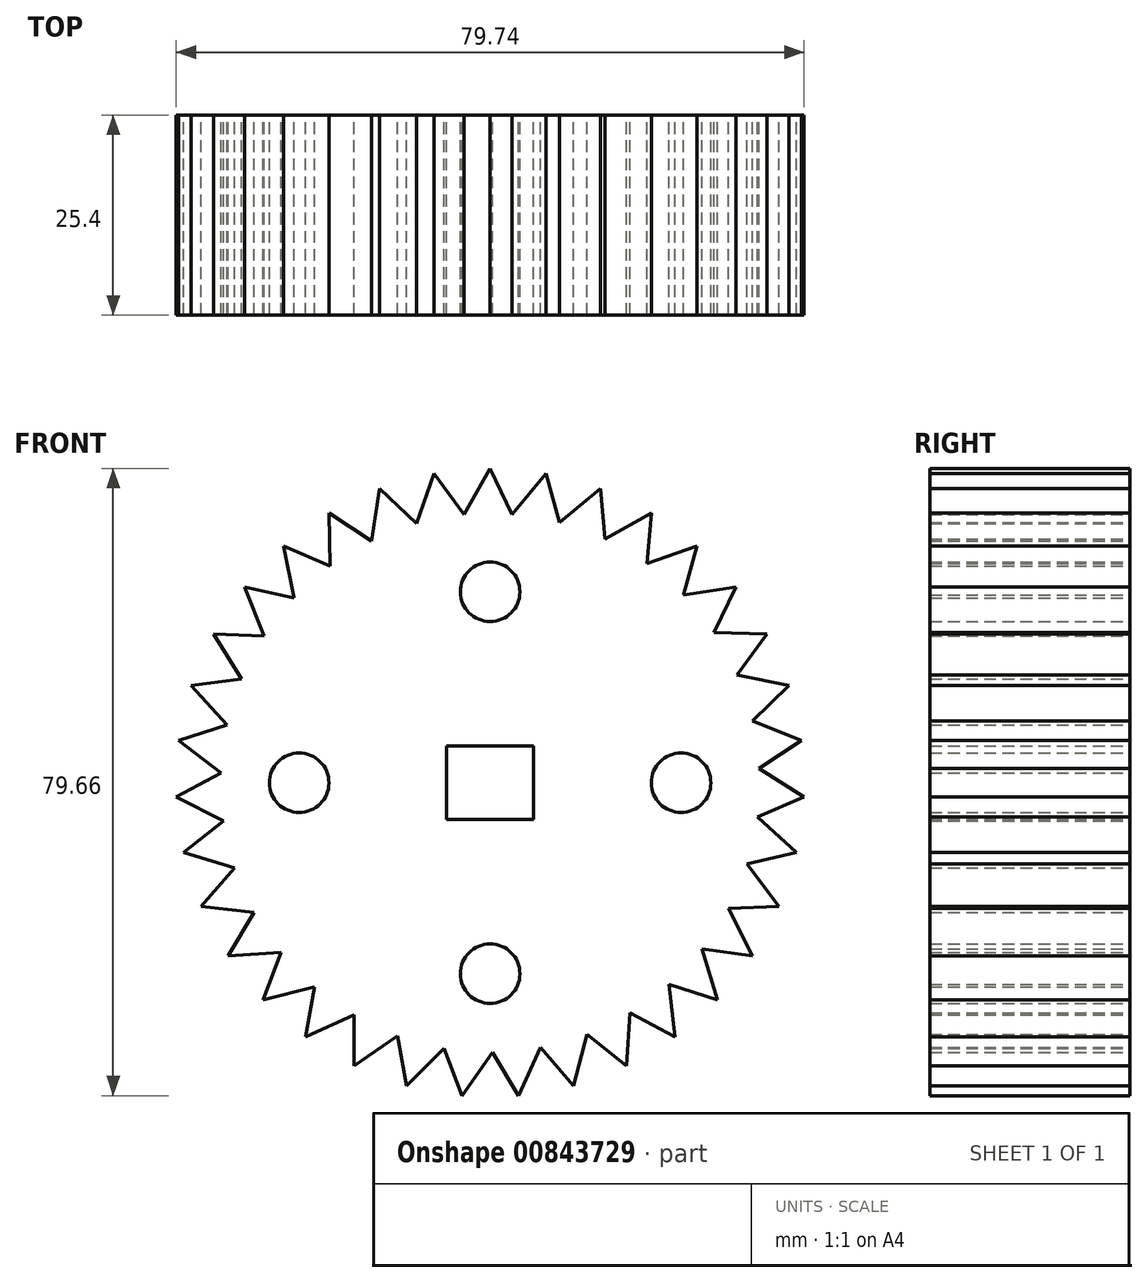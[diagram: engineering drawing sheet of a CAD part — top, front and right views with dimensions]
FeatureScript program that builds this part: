
annotation { "Feature Type Name" : "Feature", "Feature Type Description" : "" }
export const myFeature = defineFeature(function(context is Context, id is Id, definition is map)
    precondition{}
    {
        {
            var Q0;
            Q0=qCreatedBy(makeId("Front.planeOp"),FACE);
            var sketch = newSketch(context, id + "F0", { "sketchPlane" : qUnion([Q0])});
            skLineSegment(sketch, "E0.bottom", {"start": v(5.53, 4.68) * mm, "end": v(-5.53, 4.68) * mm});
            skLineSegment(sketch, "E0.top", {"start": v(5.53, -4.68) * mm, "end": v(-5.53, -4.68) * mm});
            skLineSegment(sketch, "E0.left", {"start": v(5.53, 4.68) * mm, "end": v(5.53, -4.68) * mm});
            skLineSegment(sketch, "E0.right", {"start": v(-5.53, 4.68) * mm, "end": v(-5.53, -4.68) * mm});
            skPoint(sketch, "E0.middle", {"position": v(0, 0) * mm});
            skLineSegment(sketch, "E1.bottom", {"start": v(9.22, 8.65) * mm, "end": v(-9.22, 8.65) * mm});
            skLineSegment(sketch, "E1.top", {"start": v(9.22, -8.65) * mm, "end": v(-9.22, -8.65) * mm});
            skLineSegment(sketch, "E1.left", {"start": v(9.22, 8.65) * mm, "end": v(9.22, -8.65) * mm});
            skLineSegment(sketch, "E1.right", {"start": v(-9.22, 8.65) * mm, "end": v(-9.22, -8.65) * mm});
            skLineSegment(sketch, "E2", {"start": v(-2.98, 8.65) * mm, "end": v(-2.98, 16.88) * mm});
            skLineSegment(sketch, "E3", {"start": v(2.98, 8.65) * mm, "end": v(2.98, 16.88) * mm});
            skCircle(sketch, "E4", {"center": v(0, 24.26) * mm, "radius": 3.78 * mm});
            skLineSegment(sketch, "E5.1.0", {"start": v(-8.65, 2.98) * mm, "end": v(-16.88, 2.98) * mm});
            skLineSegment(sketch, "E5.1.1", {"start": v(-8.65, -2.98) * mm, "end": v(-16.88, -2.98) * mm});
            skCircle(sketch, "E5.1.2", {"center": v(-24.26, 0) * mm, "radius": 3.78 * mm});
            skLineSegment(sketch, "E5.2.0", {"start": v(-2.98, -8.65) * mm, "end": v(-2.98, -16.88) * mm});
            skLineSegment(sketch, "E5.2.1", {"start": v(2.98, -8.65) * mm, "end": v(2.98, -16.88) * mm});
            skCircle(sketch, "E5.2.2", {"center": v(0, -24.26) * mm, "radius": 3.78 * mm});
            skLineSegment(sketch, "E5.3.0", {"start": v(8.65, -2.98) * mm, "end": v(16.88, -2.98) * mm});
            skLineSegment(sketch, "E5.3.1", {"start": v(8.65, 2.98) * mm, "end": v(16.88, 2.98) * mm});
            skCircle(sketch, "E5.3.2", {"center": v(24.26, 0) * mm, "radius": 3.78 * mm});
            skCircle(sketch, "E6", {"center": v(0, 23.4) * mm, "radius": 7.16 * mm});
            skPoint(sketch, "E6.third.point", {"position": v(0, 30.56) * mm});
            skCircle(sketch, "E7.1.0", {"center": v(-23.4, 0) * mm, "radius": 7.16 * mm});
            skCircle(sketch, "E7.2.0", {"center": v(0, -23.4) * mm, "radius": 7.16 * mm});
            skCircle(sketch, "E7.3.0", {"center": v(23.4, 0) * mm, "radius": 7.16 * mm});
            skCircle(sketch, "E8", {"center": v(0, 0) * mm, "radius": 33.5 * mm});
            skLineSegment(sketch, "E9", {"start": v(-3.78, 33.28) * mm, "end": v(0, 39.91) * mm});
            skLineSegment(sketch, "E10", {"start": v(0, 39.91) * mm, "end": v(3.16, 33.34) * mm});
            skLineSegment(sketch, "E11.1.0", {"start": v(-7.13, 39.27) * mm, "end": v(-2.84, 33.37) * mm});
            skLineSegment(sketch, "E11.1.1", {"start": v(-9.66, 32.07) * mm, "end": v(-7.13, 39.27) * mm});
            skLineSegment(sketch, "E11.2.0", {"start": v(-14.02, 37.37) * mm, "end": v(-8.76, 32.33) * mm});
            skLineSegment(sketch, "E11.2.1", {"start": v(-15.24, 29.83) * mm, "end": v(-14.02, 37.37) * mm});
            skLineSegment(sketch, "E11.3.0", {"start": v(-20.47, 34.26) * mm, "end": v(-14.39, 30.25) * mm});
            skLineSegment(sketch, "E11.3.1", {"start": v(-20.32, 26.63) * mm, "end": v(-20.47, 34.26) * mm});
            skLineSegment(sketch, "E11.4.0", {"start": v(-26.26, 30.06) * mm, "end": v(-19.56, 27.2) * mm});
            skLineSegment(sketch, "E11.4.1", {"start": v(-24.74, 22.57) * mm, "end": v(-26.26, 30.06) * mm});
            skLineSegment(sketch, "E11.5.0", {"start": v(-31.2, 24.89) * mm, "end": v(-24.1, 23.26) * mm});
            skLineSegment(sketch, "E11.5.1", {"start": v(-28.38, 17.8) * mm, "end": v(-31.2, 24.89) * mm});
            skLineSegment(sketch, "E11.6.0", {"start": v(-35.15, 18.91) * mm, "end": v(-27.86, 18.59) * mm});
            skLineSegment(sketch, "E11.6.1", {"start": v(-31.1, 12.44) * mm, "end": v(-35.15, 18.91) * mm});
            skLineSegment(sketch, "E11.7.0", {"start": v(-37.96, 12.33) * mm, "end": v(-30.74, 13.31) * mm});
            skLineSegment(sketch, "E11.7.1", {"start": v(-32.82, 6.69) * mm, "end": v(-37.96, 12.33) * mm});
            skLineSegment(sketch, "E11.8.0", {"start": v(-39.55, 5.36) * mm, "end": v(-32.62, 7.6) * mm});
            skLineSegment(sketch, "E11.8.1", {"start": v(-33.49, 0.72) * mm, "end": v(-39.55, 5.36) * mm});
            skLineSegment(sketch, "E11.9.0", {"start": v(-39.87, -1.8) * mm, "end": v(-33.45, 1.66) * mm});
            skLineSegment(sketch, "E11.9.1", {"start": v(-33.08, -5.27) * mm, "end": v(-39.87, -1.8) * mm});
            skLineSegment(sketch, "E12.2.10.0", {"start": v(-38.91, -8.88) * mm, "end": v(-33.21, -4.34) * mm});
            skLineSegment(sketch, "E12.3.10.0", {"start": v(-31.6, -11.1) * mm, "end": v(-38.91, -8.88) * mm});
            skLineSegment(sketch, "E12.2.11.0", {"start": v(-36.7, -15.69) * mm, "end": v(-31.9, -10.2) * mm});
            skLineSegment(sketch, "E12.3.11.0", {"start": v(-29.12, -16.56) * mm, "end": v(-36.7, -15.69) * mm});
            skLineSegment(sketch, "E12.2.12.0", {"start": v(-33.31, -21.99) * mm, "end": v(-29.57, -15.73) * mm});
            skLineSegment(sketch, "E12.3.12.0", {"start": v(-25.7, -21.5) * mm, "end": v(-33.31, -21.99) * mm});
            skLineSegment(sketch, "E12.2.13.0", {"start": v(-28.85, -27.58) * mm, "end": v(-26.29, -20.76) * mm});
            skLineSegment(sketch, "E12.3.13.0", {"start": v(-21.44, -25.73) * mm, "end": v(-28.85, -27.58) * mm});
            skLineSegment(sketch, "E12.2.14.0", {"start": v(-23.46, -32.3) * mm, "end": v(-22.16, -25.12) * mm});
            skLineSegment(sketch, "E12.3.14.0", {"start": v(-16.5, -29.15) * mm, "end": v(-23.46, -32.3) * mm});
            skLineSegment(sketch, "E12.2.15.0", {"start": v(-17.32, -35.96) * mm, "end": v(-17.32, -28.67) * mm});
            skLineSegment(sketch, "E12.3.15.0", {"start": v(-11.03, -31.63) * mm, "end": v(-17.32, -35.96) * mm});
            skLineSegment(sketch, "E12.2.16.0", {"start": v(-10.62, -38.47) * mm, "end": v(-11.92, -31.3) * mm});
            skLineSegment(sketch, "E12.3.16.0", {"start": v(-5.2, -33.09) * mm, "end": v(-10.62, -38.47) * mm});
            skLineSegment(sketch, "E12.2.17.0", {"start": v(-3.58, -39.75) * mm, "end": v(-6.14, -32.93) * mm});
            skLineSegment(sketch, "E12.3.17.0", {"start": v(0.78, -33.48) * mm, "end": v(-3.58, -39.75) * mm});
            skLineSegment(sketch, "E12.2.18.0", {"start": v(3.58, -39.75) * mm, "end": v(-0.16, -33.5) * mm});
            skLineSegment(sketch, "E12.3.18.0", {"start": v(6.75, -32.8) * mm, "end": v(3.58, -39.75) * mm});
            skLineSegment(sketch, "E12.2.19.0", {"start": v(10.62, -38.47) * mm, "end": v(5.82, -32.98) * mm});
            skLineSegment(sketch, "E12.3.19.0", {"start": v(12.5, -31.07) * mm, "end": v(10.62, -38.47) * mm});
            skLineSegment(sketch, "E12.2.20.0", {"start": v(17.32, -35.96) * mm, "end": v(11.62, -31.41) * mm});
            skLineSegment(sketch, "E12.3.20.0", {"start": v(17.85, -28.34) * mm, "end": v(17.32, -35.96) * mm});
            skLineSegment(sketch, "E12.2.21.0", {"start": v(23.46, -32.3) * mm, "end": v(17.04, -28.83) * mm});
            skLineSegment(sketch, "E12.3.21.0", {"start": v(22.62, -24.7) * mm, "end": v(23.46, -32.3) * mm});
            skLineSegment(sketch, "E12.2.22.0", {"start": v(28.85, -27.58) * mm, "end": v(21.92, -25.33) * mm});
            skLineSegment(sketch, "E12.3.22.0", {"start": v(26.67, -20.26) * mm, "end": v(28.85, -27.58) * mm});
            skLineSegment(sketch, "E12.2.23.0", {"start": v(33.31, -21.99) * mm, "end": v(26.09, -21) * mm});
            skLineSegment(sketch, "E12.3.23.0", {"start": v(29.86, -15.18) * mm, "end": v(33.31, -21.99) * mm});
            skLineSegment(sketch, "E12.2.24.0", {"start": v(36.7, -15.69) * mm, "end": v(29.42, -16.01) * mm});
            skLineSegment(sketch, "E12.3.24.0", {"start": v(32.09, -9.6) * mm, "end": v(36.7, -15.69) * mm});
            skLineSegment(sketch, "E12.2.25.0", {"start": v(38.91, -8.88) * mm, "end": v(31.8, -10.5) * mm});
            skLineSegment(sketch, "E12.3.25.0", {"start": v(33.29, -3.72) * mm, "end": v(38.91, -8.88) * mm});
            skLineSegment(sketch, "E12.2.26.0", {"start": v(39.87, -1.8) * mm, "end": v(33.17, -4.65) * mm});
            skLineSegment(sketch, "E12.3.26.0", {"start": v(33.42, 2.29) * mm, "end": v(39.87, -1.8) * mm});
            skLineSegment(sketch, "E12.2.27.0", {"start": v(39.55, 5.36) * mm, "end": v(33.47, 1.34) * mm});
            skLineSegment(sketch, "E12.3.27.0", {"start": v(32.47, 8.22) * mm, "end": v(39.55, 5.36) * mm});
            skLineSegment(sketch, "E12.2.28.0", {"start": v(37.96, 12.33) * mm, "end": v(32.69, 7.3) * mm});
            skLineSegment(sketch, "E12.3.28.0", {"start": v(30.48, 13.88) * mm, "end": v(37.96, 12.33) * mm});
            skLineSegment(sketch, "E12.2.29.0", {"start": v(35.15, 18.91) * mm, "end": v(30.86, 13.02) * mm});
            skLineSegment(sketch, "E12.3.29.0", {"start": v(27.51, 19.1) * mm, "end": v(35.15, 18.91) * mm});
            skLineSegment(sketch, "E13.2.30.0", {"start": v(31.2, 24.89) * mm, "end": v(28.04, 18.32) * mm});
            skLineSegment(sketch, "E13.3.30.0", {"start": v(23.66, 23.7) * mm, "end": v(31.2, 24.89) * mm});
            skLineSegment(sketch, "E13.2.31.0", {"start": v(26.26, 30.06) * mm, "end": v(24.32, 23.03) * mm});
            skLineSegment(sketch, "E13.3.31.0", {"start": v(19.05, 27.55) * mm, "end": v(26.26, 30.06) * mm});
            skLineSegment(sketch, "E13.2.32.0", {"start": v(20.47, 34.26) * mm, "end": v(19.82, 27) * mm});
            skLineSegment(sketch, "E13.3.32.0", {"start": v(13.82, 30.5) * mm, "end": v(20.47, 34.26) * mm});
            skLineSegment(sketch, "E13.2.33.0", {"start": v(14.02, 37.37) * mm, "end": v(14.68, 30.1) * mm});
            skLineSegment(sketch, "E13.3.33.0", {"start": v(8.15, 32.49) * mm, "end": v(14.02, 37.37) * mm});
            skLineSegment(sketch, "E13.2.34.0", {"start": v(7.13, 39.27) * mm, "end": v(9.07, 32.24) * mm});
            skLineSegment(sketch, "E13.3.34.0", {"start": v(2.22, 33.42) * mm, "end": v(7.13, 39.27) * mm});
            skSolve(sketch);
        }
        {
            var Q0;
            Q0 = qSketchRegion(id + "F0", true);
            var Q1;
            {var subQ23=sQuery(id+"F0.wireOp",EDGE,"E2");Q1=makeQuery(id+"F0.imprint","IMPRINT",FACE,{"disambiguationData":[TD([[makeQuery(id+"F0.imprint","IMPRINT",EDGE,{"derivedFrom":subQ23}),1.0]])]});}
            var Q2;
            Q2=makeQuery(id+"F0.imprint","IMPRINT",FACE,{"disambiguationData":[TD([[makeQuery(id+"F0.imprint","IMPRINT",EDGE,{"derivedFrom":sQuery(id+"F0.wireOp",EDGE,"E0.bottom")}),-1.0]])]});
            var Q3;
            {var subQ0=sQuery(id+"F0.wireOp",EDGE,"E5.1.0");var subQ1=sQuery(id+"F0.wireOp",EDGE,"E1.right");var subQ2=makeQuery(id+"F0.imprint","INTERSECT",VERTEX,{"derivedFrom":[subQ1,subQ0]});Q3=makeQuery(id+"F0.imprint","IMPRINT",FACE,{"disambiguationData":[TD([[makeQuery(id+"F0.imprint","IMPRINT",EDGE,{"disambiguationData":[TD([[subQ2,-1.0]])],"derivedFrom":subQ1}),-1.0]])]});}
            var Q4;
            Q4=makeQuery(id+"F0.imprint","IMPRINT",FACE,{"disambiguationData":[TD([[makeQuery(id+"F0.imprint","IMPRINT",EDGE,{"derivedFrom":sQuery(id+"F0.wireOp",EDGE,"E5.1.2")}),-1.0]])]});
            var Q5;
            {var subQ0=sQuery(id+"F0.wireOp",EDGE,"E5.2.0");Q5=makeQuery(id+"F0.imprint","IMPRINT",FACE,{"disambiguationData":[TD([[makeQuery(id+"F0.imprint","IMPRINT",EDGE,{"derivedFrom":subQ0}),1.0]])]});}
            var Q6;
            {var subQ0=sQuery(id+"F0.wireOp",EDGE,"E5.3.1");var subQ1=sQuery(id+"F0.wireOp",EDGE,"E1.left");var subQ2=makeQuery(id+"F0.imprint","INTERSECT",VERTEX,{"derivedFrom":[subQ1,subQ0]});Q6=makeQuery(id+"F0.imprint","IMPRINT",FACE,{"disambiguationData":[TD([[makeQuery(id+"F0.imprint","IMPRINT",EDGE,{"disambiguationData":[TD([[subQ2,-1.0]])],"derivedFrom":subQ1}),1.0]])]});}
            var Q7;
            {var subQ0=sQuery(id+"F0.wireOp",EDGE,"E2");Q7=makeQuery(id+"F0.imprint","IMPRINT",FACE,{"disambiguationData":[TD([[makeQuery(id+"F0.imprint","IMPRINT",EDGE,{"derivedFrom":subQ0}),-1.0]])]});}
            var Q8;
            Q8=makeQuery(id+"F0.imprint","IMPRINT",FACE,{"disambiguationData":[TD([[makeQuery(id+"F0.imprint","IMPRINT",EDGE,{"derivedFrom":sQuery(id+"F0.wireOp",EDGE,"E4")}),-1.0]])]});
            var Q9;
            Q9=makeQuery(id+"F0.imprint","IMPRINT",FACE,{"disambiguationData":[TD([[makeQuery(id+"F0.imprint","IMPRINT",EDGE,{"derivedFrom":sQuery(id+"F0.wireOp",EDGE,"E5.2.2")}),-1.0]])]});
            var Q10;
            Q10=makeQuery(id+"F0.imprint","IMPRINT",FACE,{"disambiguationData":[TD([[makeQuery(id+"F0.imprint","IMPRINT",EDGE,{"derivedFrom":sQuery(id+"F0.wireOp",EDGE,"E5.3.2")}),-1.0]])]});
            extrude(context, id + "F1", {"entities" : qUnion([Q0, Q1, Q2, Q3, Q4, Q5, Q6, Q7, Q8, Q9, Q10]), "depth" : 25.4 * mm, "offsetDistance" : 25.4 * mm});
        }
    });
